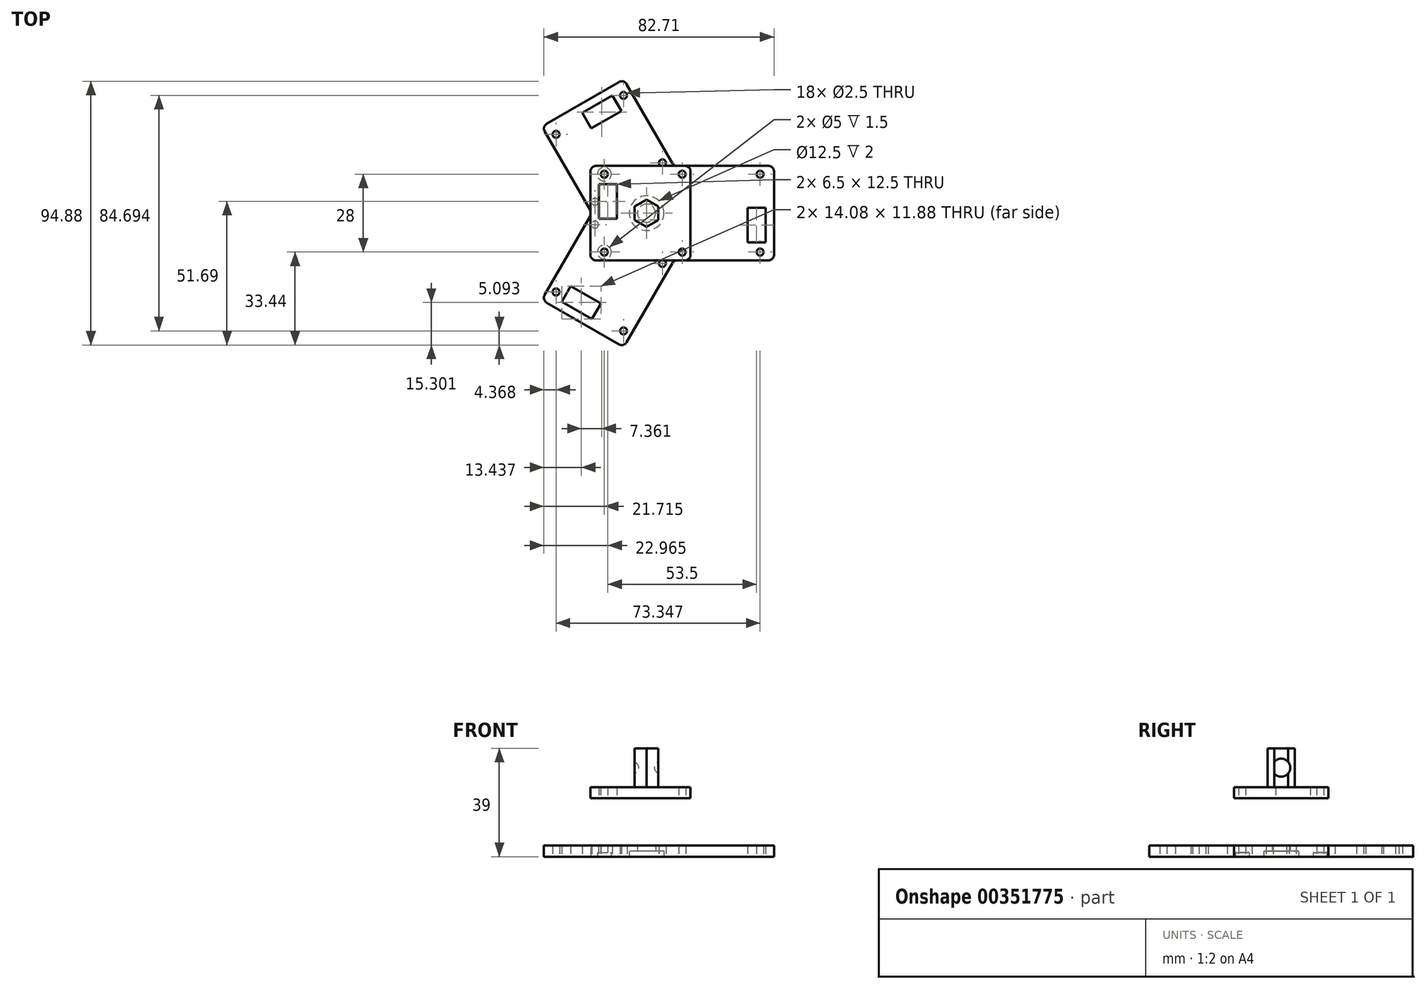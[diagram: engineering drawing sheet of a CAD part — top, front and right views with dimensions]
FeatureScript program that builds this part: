
annotation { "Feature Type Name" : "Feature", "Feature Type Description" : "" }
export const myFeature = defineFeature(function(context is Context, id is Id, definition is map)
    precondition{}
    {
        {
            var Q0;
            Q0=qCreatedBy(makeId("Top.planeOp"),FACE);
            var sketch = newSketch(context, id + "F0", { "sketchPlane" : qUnion([Q0])});
            skCircle(sketch, "E0.cCircle", {"center": v(0, 0) * mm, "radius": 9.81 * mm, "construction": true});
            skLineSegment(sketch, "E0.0", {"start": v(9.81, 17) * mm, "end": v(9.81, -17) * mm});
            skLineSegment(sketch, "E0.1", {"start": v(9.81, -17) * mm, "end": v(-19.63, 0) * mm});
            skLineSegment(sketch, "E0.2", {"start": v(-19.63, 0) * mm, "end": v(9.81, 17) * mm});
            skPoint(sketch, "E0.0.midPoint", {"position": v(9.81, 0) * mm});
            skLineSegment(sketch, "E1.bottom", {"start": v(9.81, -17) * mm, "end": v(45.81, -17) * mm});
            skLineSegment(sketch, "E1.top", {"start": v(9.81, 17) * mm, "end": v(45.81, 17) * mm});
            skLineSegment(sketch, "E1.left", {"start": v(9.81, -17) * mm, "end": v(9.81, 17) * mm});
            skLineSegment(sketch, "E1.right", {"start": v(45.81, -17) * mm, "end": v(45.81, 17) * mm});
            skLineSegment(sketch, "E2", {"start": v(9.81, 17) * mm, "end": v(-8.19, 48.18) * mm});
            skLineSegment(sketch, "E3", {"start": v(-8.19, 48.18) * mm, "end": v(-37.63, 31.18) * mm});
            skLineSegment(sketch, "E4", {"start": v(-37.63, 31.18) * mm, "end": v(-19.63, 0) * mm});
            skLineSegment(sketch, "E5", {"start": v(-19.63, 0) * mm, "end": v(-37.63, -31.18) * mm});
            skLineSegment(sketch, "E6", {"start": v(-37.63, -31.18) * mm, "end": v(-8.19, -48.18) * mm});
            skLineSegment(sketch, "E7", {"start": v(-8.19, -48.18) * mm, "end": v(9.81, -17) * mm});
            skCircle(sketch, "E8", {"center": v(0, 0) * mm, "radius": 3.25 * mm});
            skLineSegment(sketch, "E9", {"start": v(-19.63, 0) * mm, "end": v(-19.63, 0) * mm});
            skLineSegment(sketch, "E10", {"start": v(9.81, -17) * mm, "end": v(9.81, -17) * mm});
            skCircle(sketch, "E11", {"center": v(0, 0) * mm, "radius": 6.25 * mm});
            skCircle(sketch, "E12", {"center": v(40.81, 14) * mm, "radius": 1.25 * mm});
            skCircle(sketch, "E13", {"center": v(12.81, -14) * mm, "radius": 1.25 * mm});
            skCircle(sketch, "E14", {"center": v(40.81, -14) * mm, "radius": 1.25 * mm});
            skLineSegment(sketch, "E15", {"start": v(9.81, 17) * mm, "end": v(45.81, -17) * mm, "construction": true});
            skLineSegment(sketch, "E16", {"start": v(9.81, -17) * mm, "end": v(45.81, 17) * mm, "construction": true});
            skLineSegment(sketch, "E17", {"start": v(27.81, 0) * mm, "end": v(0, 0) * mm, "construction": true});
            skCircle(sketch, "E18", {"center": v(12.81, 14) * mm, "radius": 1.25 * mm});
            skLineSegment(sketch, "E19.bottom", {"start": v(36.31, -10.5) * mm, "end": v(42.81, -10.5) * mm});
            skLineSegment(sketch, "E19.top", {"start": v(36.31, 2) * mm, "end": v(42.81, 2) * mm});
            skLineSegment(sketch, "E19.left", {"start": v(36.31, -10.5) * mm, "end": v(36.31, 2) * mm});
            skLineSegment(sketch, "E19.right", {"start": v(42.81, -10.5) * mm, "end": v(42.81, 2) * mm});
            skCircle(sketch, "E20.1.0", {"center": v(-8.28, 42.35) * mm, "radius": 1.25 * mm});
            skCircle(sketch, "E20.1.1", {"center": v(-32.53, 28.35) * mm, "radius": 1.25 * mm});
            skCircle(sketch, "E20.1.2", {"center": v(5.72, 18.1) * mm, "radius": 1.25 * mm});
            skCircle(sketch, "E20.1.3", {"center": v(-18.53, 4.1) * mm, "radius": 1.25 * mm});
            skLineSegment(sketch, "E20.1.4", {"start": v(-19.89, 30.45) * mm, "end": v(-23.14, 36.08) * mm});
            skLineSegment(sketch, "E20.1.5", {"start": v(-9.06, 36.7) * mm, "end": v(-19.89, 30.45) * mm});
            skLineSegment(sketch, "E20.1.6", {"start": v(-9.06, 36.7) * mm, "end": v(-12.31, 42.33) * mm});
            skLineSegment(sketch, "E20.1.7", {"start": v(-12.31, 42.33) * mm, "end": v(-23.14, 36.08) * mm});
            skCircle(sketch, "E20.2.0", {"center": v(-32.53, -28.35) * mm, "radius": 1.25 * mm});
            skCircle(sketch, "E20.2.1", {"center": v(-8.28, -42.35) * mm, "radius": 1.25 * mm});
            skCircle(sketch, "E20.2.2", {"center": v(-18.53, -4.1) * mm, "radius": 1.25 * mm});
            skCircle(sketch, "E20.2.3", {"center": v(5.72, -18.1) * mm, "radius": 1.25 * mm});
            skLineSegment(sketch, "E20.2.4", {"start": v(-16.43, -32.45) * mm, "end": v(-19.68, -38.08) * mm});
            skLineSegment(sketch, "E20.2.5", {"start": v(-27.25, -26.2) * mm, "end": v(-16.43, -32.45) * mm});
            skLineSegment(sketch, "E20.2.6", {"start": v(-27.25, -26.2) * mm, "end": v(-30.5, -31.83) * mm});
            skLineSegment(sketch, "E20.2.7", {"start": v(-30.5, -31.83) * mm, "end": v(-19.68, -38.08) * mm});
            skSolve(sketch);
        }
        {
            var Q0;
            Q0=makeQuery(id+"F0.imprint","IMPRINT",FACE,{"disambiguationData":[TD([[makeQuery(id+"F0.imprint","IMPRINT",EDGE,{"derivedFrom":sQuery(id+"F0.wireOp",EDGE,"E0.2")}),1.0]])]});
            var Q1;
            Q1=makeQuery(id+"F0.imprint","IMPRINT",FACE,{"disambiguationData":[TD([[makeQuery(id+"F0.imprint","IMPRINT",EDGE,{"derivedFrom":sQuery(id+"F0.wireOp",EDGE,"E1.bottom")}),1.0]])]});
            var Q2;
            Q2=makeQuery(id+"F0.imprint","IMPRINT",FACE,{"disambiguationData":[TD([[makeQuery(id+"F0.imprint","IMPRINT",EDGE,{"derivedFrom":sQuery(id+"F0.wireOp",EDGE,"E0.1")}),1.0]])]});
            var Q3;
            Q3=makeQuery(id+"F0.imprint","IMPRINT",FACE,{"disambiguationData":[TD([[makeQuery(id+"F0.imprint","IMPRINT",EDGE,{"derivedFrom":sQuery(id+"F0.wireOp",EDGE,"E0.1")}),-1.0]])]});
            var Q4;
            Q4=makeQuery(id+"F0.imprint","IMPRINT",FACE,{"disambiguationData":[TD([[makeQuery(id+"F0.imprint","IMPRINT",EDGE,{"derivedFrom":sQuery(id+"F0.wireOp",EDGE,"E8")}),-1.0]])]});
            extrude(context, id + "F1", {"entities" : qUnion([Q0, Q1, Q2, Q3, Q4]), "depth" : 4 * mm, "offsetDistance" : 25 * mm});
        }
        {
            var Q0;
            Q0=makeQuery(id+"F0.imprint","IMPRINT",FACE,{"disambiguationData":[TD([[makeQuery(id+"F0.imprint","IMPRINT",EDGE,{"derivedFrom":sQuery(id+"F0.wireOp",EDGE,"E8")}),-1.0]])]});
            extrude(context, id + "F2", {"entities" : qUnion([Q0]), "operationType" : NewBodyOperationType.REMOVE, "depth" : 2 * mm, "offsetDistance" : 25 * mm});
        }
        {
            var Q0;
            Q0=makeQuery(id+"F1.opExtrude","SWEPT_EDGE",EDGE,{"disambiguationData":[OSD([sQuery(id+"F0.wireOp",EDGE,"E2"),sQuery(id+"F0.wireOp",EDGE,"E3")])]});
            var Q1;
            Q1=makeQuery(id+"F1.opExtrude","SWEPT_EDGE",EDGE,{"disambiguationData":[OSD([sQuery(id+"F0.wireOp",EDGE,"E1.top"),sQuery(id+"F0.wireOp",EDGE,"E1.right")])]});
            var Q2;
            Q2=makeQuery(id+"F1.opExtrude","SWEPT_EDGE",EDGE,{"disambiguationData":[OSD([sQuery(id+"F0.wireOp",EDGE,"E1.bottom"),sQuery(id+"F0.wireOp",EDGE,"E1.right")])]});
            var Q3;
            Q3=makeQuery(id+"F1.opExtrude","SWEPT_EDGE",EDGE,{"disambiguationData":[OSD([sQuery(id+"F0.wireOp",EDGE,"E0.1"),sQuery(id+"F0.wireOp",EDGE,"E1.bottom"),sQuery(id+"F0.wireOp",EDGE,"E1.left"),sQuery(id+"F0.wireOp",EDGE,"E7")])]});
            var Q4;
            Q4=makeQuery(id+"F1.opExtrude","SWEPT_EDGE",EDGE,{"disambiguationData":[OSD([sQuery(id+"F0.wireOp",EDGE,"E6"),sQuery(id+"F0.wireOp",EDGE,"E7")])]});
            var Q5;
            Q5=makeQuery(id+"F1.opExtrude","SWEPT_EDGE",EDGE,{"disambiguationData":[OSD([sQuery(id+"F0.wireOp",EDGE,"E5"),sQuery(id+"F0.wireOp",EDGE,"E6")])]});
            var Q6;
            Q6=makeQuery(id+"F1.opExtrude","SWEPT_EDGE",EDGE,{"disambiguationData":[OSD([sQuery(id+"F0.wireOp",EDGE,"E0.1"),sQuery(id+"F0.wireOp",EDGE,"E0.2"),sQuery(id+"F0.wireOp",EDGE,"E4"),sQuery(id+"F0.wireOp",EDGE,"E5")])]});
            var Q7;
            Q7=makeQuery(id+"F1.opExtrude","SWEPT_EDGE",EDGE,{"disambiguationData":[OSD([sQuery(id+"F0.wireOp",EDGE,"E3"),sQuery(id+"F0.wireOp",EDGE,"E4")])]});
            var Q8;
            Q8=makeQuery(id+"F1.opExtrude","SWEPT_EDGE",EDGE,{"disambiguationData":[OSD([sQuery(id+"F0.wireOp",EDGE,"E0.2"),sQuery(id+"F0.wireOp",EDGE,"E1.top"),sQuery(id+"F0.wireOp",EDGE,"E1.left"),sQuery(id+"F0.wireOp",EDGE,"E2")])]});
            fillet(context, id + "F3", {"entities" : qUnion([Q0, Q1, Q2, Q3, Q4, Q5, Q6, Q7, Q8]), "radius" : 2 * mm, "tangentPropagation" : true, "allowEdgeOverflow" : false});
        }
        {
            var Q0;
            Q0=qCreatedBy(makeId("Top.planeOp"),FACE);
            var sketch = newSketch(context, id + "F4", { "sketchPlane" : qUnion([Q0])});
            skPoint(sketch, "E21.0.midPoint", {"position": v(18, 0) * mm});
            skLineSegment(sketch, "E22.bottom", {"start": v(15.81, 17) * mm, "end": v(-20.19, 17) * mm});
            skLineSegment(sketch, "E22.top", {"start": v(15.81, -17) * mm, "end": v(-20.19, -17) * mm});
            skLineSegment(sketch, "E22.left", {"start": v(15.81, 17) * mm, "end": v(15.81, -17) * mm});
            skLineSegment(sketch, "E22.right", {"start": v(-20.19, 17) * mm, "end": v(-20.19, -17) * mm});
            skCircle(sketch, "E23", {"center": v(-15.19, -14) * mm, "radius": 1.25 * mm});
            skCircle(sketch, "E24", {"center": v(12.81, 14) * mm, "radius": 1.25 * mm});
            skCircle(sketch, "E25", {"center": v(-15.19, 14) * mm, "radius": 1.25 * mm});
            skLineSegment(sketch, "E26", {"start": v(15.81, -17) * mm, "end": v(-20.19, 17) * mm, "construction": true});
            skLineSegment(sketch, "E27", {"start": v(15.81, 17) * mm, "end": v(-20.19, -17) * mm, "construction": true});
            skLineSegment(sketch, "E28", {"start": v(-2.19, 0) * mm, "end": v(25.63, 0) * mm, "construction": true});
            skCircle(sketch, "E29", {"center": v(12.81, -14) * mm, "radius": 1.25 * mm});
            skLineSegment(sketch, "E30.bottom", {"start": v(-10.69, 10.5) * mm, "end": v(-17.19, 10.5) * mm});
            skLineSegment(sketch, "E30.top", {"start": v(-10.69, -2) * mm, "end": v(-17.19, -2) * mm});
            skLineSegment(sketch, "E30.left", {"start": v(-10.69, 10.5) * mm, "end": v(-10.69, -2) * mm});
            skLineSegment(sketch, "E30.right", {"start": v(-17.19, 10.5) * mm, "end": v(-17.19, -2) * mm});
            skSolve(sketch);
        }
        {
            var Q0;
            Q0 = qSketchRegion(id + "F4", true);
            extrude(context, id + "F5", {"entities" : qUnion([Q0]), "depth" : 25 * mm, "offsetDistance" : 25 * mm, "hasSecondDirection" : true, "secondDirectionOppositeDirection" : false, "secondDirectionDepth" : 21 * mm});
        }
        {
            var Q0;
            Q0=sQuery(id+"F4.wireOp",VERTEX,"E25.center");
            var Q1;
            Q1=sQuery(id+"F4.wireOp",VERTEX,"E23.center");
            var Q2;
            Q2=makeQuery(id+"F1.opExtrude","SWEPT_BODY",BODY,{"disambiguationData":[OSD([sQuery(id+"F0.wireOp",EDGE,"E1.bottom"),sQuery(id+"F0.wireOp",EDGE,"E1.top"),sQuery(id+"F0.wireOp",EDGE,"E1.right"),sQuery(id+"F0.wireOp",EDGE,"E2"),sQuery(id+"F0.wireOp",EDGE,"E3"),sQuery(id+"F0.wireOp",EDGE,"E4"),sQuery(id+"F0.wireOp",EDGE,"E5"),sQuery(id+"F0.wireOp",EDGE,"E6"),sQuery(id+"F0.wireOp",EDGE,"E7"),sQuery(id+"F0.wireOp",EDGE,"E8"),sQuery(id+"F0.wireOp",EDGE,"E12"),sQuery(id+"F0.wireOp",EDGE,"E13"),sQuery(id+"F0.wireOp",EDGE,"E14"),sQuery(id+"F0.wireOp",EDGE,"E18"),sQuery(id+"F0.wireOp",EDGE,"E19.bottom"),sQuery(id+"F0.wireOp",EDGE,"E19.top"),sQuery(id+"F0.wireOp",EDGE,"E19.left"),sQuery(id+"F0.wireOp",EDGE,"E19.right"),sQuery(id+"F0.wireOp",EDGE,"E20.1.0"),sQuery(id+"F0.wireOp",EDGE,"E20.1.1"),sQuery(id+"F0.wireOp",EDGE,"E20.1.2"),sQuery(id+"F0.wireOp",EDGE,"E20.1.3"),sQuery(id+"F0.wireOp",EDGE,"E20.1.4"),sQuery(id+"F0.wireOp",EDGE,"E20.1.5"),sQuery(id+"F0.wireOp",EDGE,"E20.1.6"),sQuery(id+"F0.wireOp",EDGE,"E20.1.7"),sQuery(id+"F0.wireOp",EDGE,"E20.2.0"),sQuery(id+"F0.wireOp",EDGE,"E20.2.1"),sQuery(id+"F0.wireOp",EDGE,"E20.2.2"),sQuery(id+"F0.wireOp",EDGE,"E20.2.3"),sQuery(id+"F0.wireOp",EDGE,"E20.2.4"),sQuery(id+"F0.wireOp",EDGE,"E20.2.5"),sQuery(id+"F0.wireOp",EDGE,"E20.2.6"),sQuery(id+"F0.wireOp",EDGE,"E20.2.7")])]});
            var Q3;
            Q3=makeQuery(id+"F5.opExtrude","SWEPT_BODY",BODY,{"disambiguationData":[OSD([sQuery(id+"F4.wireOp",EDGE,"E22.bottom"),sQuery(id+"F4.wireOp",EDGE,"E22.top"),sQuery(id+"F4.wireOp",EDGE,"E22.left"),sQuery(id+"F4.wireOp",EDGE,"E22.right"),sQuery(id+"F4.wireOp",EDGE,"E23"),sQuery(id+"F4.wireOp",EDGE,"E24"),sQuery(id+"F4.wireOp",EDGE,"E25"),sQuery(id+"F4.wireOp",EDGE,"E29"),sQuery(id+"F4.wireOp",EDGE,"E30.bottom"),sQuery(id+"F4.wireOp",EDGE,"E30.top"),sQuery(id+"F4.wireOp",EDGE,"E30.left"),sQuery(id+"F4.wireOp",EDGE,"E30.right")])]});
            hole(context, id + "F6", {"style" : HoleStyle.C_BORE, "endStyle" : HoleEndStyle.THROUGH, "oppositeDirection" : true, "holeDiameter" : 2.5 * mm, "cBoreDiameter" : 5 * mm, "cBoreDepth" : 1.5 * mm, "majorDiameter" : 5 * mm, "isTappedThrough" : true, "tappedDepth" : 12 * mm, "tapClearance" : 3, "locations" : qUnion([Q0, Q1]), "scope" : qUnion([Q2, Q3])});
        }
        {
            var Q0;
            Q0=makeQuery(id+"F5.opExtrude","CAP_FACE",FACE,{"disambiguationData":[OSD([sQuery(id+"F4.wireOp",EDGE,"E22.bottom"),sQuery(id+"F4.wireOp",EDGE,"E22.top"),sQuery(id+"F4.wireOp",EDGE,"E22.left"),sQuery(id+"F4.wireOp",EDGE,"E22.right"),sQuery(id+"F4.wireOp",EDGE,"E23"),sQuery(id+"F4.wireOp",EDGE,"E24"),sQuery(id+"F4.wireOp",EDGE,"E25"),sQuery(id+"F4.wireOp",EDGE,"E29"),sQuery(id+"F4.wireOp",EDGE,"E30.bottom"),sQuery(id+"F4.wireOp",EDGE,"E30.top"),sQuery(id+"F4.wireOp",EDGE,"E30.left"),sQuery(id+"F4.wireOp",EDGE,"E30.right")])],"isStart":false});
            var sketch = newSketch(context, id + "F7", { "sketchPlane" : qUnion([Q0])});
            skCircle(sketch, "E31.cCircle", {"center": v(0, 0) * mm, "radius": 4.25 * mm, "construction": true});
            skLineSegment(sketch, "E31.0", {"start": v(4.25, 2.45) * mm, "end": v(4.25, -2.45) * mm});
            skLineSegment(sketch, "E31.1", {"start": v(4.25, -2.45) * mm, "end": v(0, -4.9) * mm});
            skLineSegment(sketch, "E31.2", {"start": v(0, -4.9) * mm, "end": v(-4.25, -2.45) * mm});
            skLineSegment(sketch, "E31.3", {"start": v(-4.25, -2.45) * mm, "end": v(-4.25, 2.45) * mm});
            skLineSegment(sketch, "E31.4", {"start": v(-4.25, 2.45) * mm, "end": v(0, 4.9) * mm});
            skLineSegment(sketch, "E31.5", {"start": v(0, 4.9) * mm, "end": v(4.25, 2.45) * mm});
            skPoint(sketch, "E31.0.midPoint", {"position": v(4.25, 0) * mm});
            skSolve(sketch);
        }
        {
            var Q0;
            Q0=makeQuery(id+"F7.imprint","IMPRINT",FACE,{"disambiguationData":[TD([[makeQuery(id+"F7.imprint","IMPRINT",EDGE,{"derivedFrom":sQuery(id+"F7.wireOp",EDGE,"E31.0")}),-1.0]])]});
            extrude(context, id + "F8", {"entities" : qUnion([Q0]), "operationType" : NewBodyOperationType.ADD, "depth" : 14 * mm, "offsetDistance" : 25 * mm});
        }
        {
            var Q0;
            Q0=makeQuery(id+"F8.opExtrude","SWEPT_FACE",FACE,{"disambiguationData":[OSD([sQuery(id+"F7.wireOp",EDGE,"E31.3")])]});
            var sketch = newSketch(context, id + "F9", { "sketchPlane" : qUnion([Q0])});
            skPoint(sketch, "E32.centerSnap0", {"position": v(0, 25) * mm});
            skLineSegment(sketch, "E33", {"start": v(-2.45, 32) * mm, "end": v(-5.49, 32) * mm, "construction": true});
            skCircle(sketch, "E34", {"center": v(0, 32) * mm, "radius": 3.25 * mm});
            skCircle(sketch, "E35", {"center": v(0, 32) * mm, "radius": 7 * mm});
            skSolve(sketch);
        }
        {
            var Q0;
            {var subQ0=sQuery(id+"F9.wireOp",EDGE,"E34");var subQ1=sQuery(id+"F7.wireOp",EDGE,"E31.0");var subQ2=makeQuery(id+"F8.opExtrude","SWEPT_EDGE",EDGE,{"disambiguationData":[OSD([subQ1,sQuery(id+"F7.wireOp",EDGE,"E31.1")])]});var subQ3=makeQuery(id+"F9.imprint","INTERSECT",VERTEX,{"disambiguationData":[OD(0.0)],"derivedFrom":[subQ2,subQ0]});Q0=makeQuery(id+"F9.imprint","IMPRINT",FACE,{"disambiguationData":[TD([[makeQuery(id+"F9.imprint","IMPRINT",EDGE,{"disambiguationData":[TD([[subQ3,1.0]])],"derivedFrom":subQ0}),1.0]])]});}
            var Q1;
            {var subQ0=sQuery(id+"F9.wireOp",EDGE,"E34");var subQ1=makeQuery(id+"F8.opExtrude","SWEPT_EDGE",EDGE,{"disambiguationData":[OSD([sQuery(id+"F7.wireOp",EDGE,"E31.0"),sQuery(id+"F7.wireOp",EDGE,"E31.1")])]});var subQ2=makeQuery(id+"F9.imprint","INTERSECT",VERTEX,{"disambiguationData":[OD(0.0)],"derivedFrom":[subQ1,subQ0]});Q1=makeQuery(id+"F9.imprint","IMPRINT",FACE,{"disambiguationData":[TD([[makeQuery(id+"F9.imprint","IMPRINT",EDGE,{"disambiguationData":[TD([[subQ2,-1.0]])],"derivedFrom":subQ0}),1.0]])]});}
            var Q2;
            {var subQ0=sQuery(id+"F9.wireOp",EDGE,"E34");var subQ1=makeQuery(id+"F8.opExtrude","SWEPT_EDGE",EDGE,{"disambiguationData":[OSD([sQuery(id+"F7.wireOp",EDGE,"E31.0"),sQuery(id+"F7.wireOp",EDGE,"E31.5")])]});var subQ2=makeQuery(id+"F9.imprint","INTERSECT",VERTEX,{"disambiguationData":[OD(0.0)],"derivedFrom":[subQ1,subQ0]});Q2=makeQuery(id+"F9.imprint","IMPRINT",FACE,{"disambiguationData":[TD([[makeQuery(id+"F9.imprint","IMPRINT",EDGE,{"disambiguationData":[TD([[subQ2,1.0]])],"derivedFrom":subQ0}),1.0]])]});}
            var Q3;
            {var subQ0=sQuery(id+"F9.wireOp",EDGE,"E34");var subQ1=makeQuery(id+"F8.opExtrude","SWEPT_EDGE",EDGE,{"disambiguationData":[OSD([sQuery(id+"F7.wireOp",EDGE,"E31.3"),sQuery(id+"F7.wireOp",EDGE,"E31.4")])]});var subQ2=makeQuery(id+"F9.imprint","INTERSECT",VERTEX,{"disambiguationData":[OD(0.0)],"derivedFrom":[subQ1,subQ0]});Q3=makeQuery(id+"F9.imprint","IMPRINT",FACE,{"disambiguationData":[TD([[makeQuery(id+"F9.imprint","IMPRINT",EDGE,{"disambiguationData":[TD([[subQ2,-1.0]])],"derivedFrom":subQ0}),1.0]])]});}
            var Q4;
            {var subQ0=sQuery(id+"F9.wireOp",EDGE,"E34");var subQ1=sQuery(id+"F7.wireOp",EDGE,"E31.3");var subQ2=makeQuery(id+"F8.opExtrude","SWEPT_EDGE",EDGE,{"disambiguationData":[OSD([subQ1,sQuery(id+"F7.wireOp",EDGE,"E31.4")])]});var subQ3=makeQuery(id+"F9.imprint","INTERSECT",VERTEX,{"disambiguationData":[OD(0.0)],"derivedFrom":[subQ2,subQ0]});Q4=makeQuery(id+"F9.imprint","IMPRINT",FACE,{"disambiguationData":[TD([[makeQuery(id+"F9.imprint","IMPRINT",EDGE,{"disambiguationData":[TD([[subQ3,1.0]])],"derivedFrom":subQ0}),1.0]])]});}
            var Q5;
            {var subQ0=sQuery(id+"F9.wireOp",EDGE,"E34");var subQ1=makeQuery(id+"F8.opExtrude","SWEPT_EDGE",EDGE,{"disambiguationData":[OSD([sQuery(id+"F7.wireOp",EDGE,"E31.2"),sQuery(id+"F7.wireOp",EDGE,"E31.3")])]});var subQ2=makeQuery(id+"F9.imprint","INTERSECT",VERTEX,{"disambiguationData":[OD(0.0)],"derivedFrom":[subQ1,subQ0]});Q5=makeQuery(id+"F9.imprint","IMPRINT",FACE,{"disambiguationData":[TD([[makeQuery(id+"F9.imprint","IMPRINT",EDGE,{"disambiguationData":[TD([[subQ2,1.0]])],"derivedFrom":subQ0}),1.0]])]});}
            extrude(context, id + "F10", {"entities" : qUnion([Q0, Q1, Q2, Q3, Q4, Q5]), "operationType" : NewBodyOperationType.REMOVE, "oppositeDirection" : true, "depth" : 25 * mm, "offsetDistance" : 25 * mm});
        }
        {
            var Q0;
            Q0=makeQuery(id+"F5.opExtrude","SWEPT_EDGE",EDGE,{"disambiguationData":[OSD([sQuery(id+"F4.wireOp",EDGE,"E22.top"),sQuery(id+"F4.wireOp",EDGE,"E22.left")])]});
            var Q1;
            Q1=makeQuery(id+"F5.opExtrude","SWEPT_EDGE",EDGE,{"disambiguationData":[OSD([sQuery(id+"F4.wireOp",EDGE,"E22.bottom"),sQuery(id+"F4.wireOp",EDGE,"E22.left")])]});
            var Q2;
            Q2=makeQuery(id+"F5.opExtrude","SWEPT_EDGE",EDGE,{"disambiguationData":[OSD([sQuery(id+"F4.wireOp",EDGE,"E22.bottom"),sQuery(id+"F4.wireOp",EDGE,"E22.right")])]});
            var Q3;
            Q3=makeQuery(id+"F5.opExtrude","SWEPT_EDGE",EDGE,{"disambiguationData":[OSD([sQuery(id+"F4.wireOp",EDGE,"E22.top"),sQuery(id+"F4.wireOp",EDGE,"E22.right")])]});
            fillet(context, id + "F11", {"entities" : qUnion([Q0, Q1, Q2, Q3]), "radius" : 2 * mm, "tangentPropagation" : true, "allowEdgeOverflow" : false});
        }
    });
